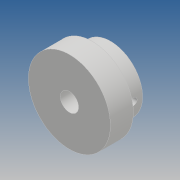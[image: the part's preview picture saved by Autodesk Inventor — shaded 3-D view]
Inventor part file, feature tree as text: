
AUTODESK INVENTOR PART (.ipt)
format: ipt  version: 2017 (Build 210142000, 142)  size: 162,816 bytes
history: native  units: mm
features: extrude x4, sketch x3, other x1, projected_geometry x1
ambient origin geometry x8: Origin, YZ Plane, XZ Plane, XY Plane, X Axis, Y Axis, Z Axis, Center Point
bodies: Body1 (feature_tree)
feature tree (9):
  other  "Sólido1"
  extrude  "Extrusión1"  Depth=10.0mm
  sketch  "Boceto2"  dims[d3=5.0mm d4=3.0mm]
  extrude  "Extrusión2"  Depth=3.0mm
  extrude  "Extrusión3"  Depth=10.0mm
  extrude  "Extrusión4"  TaperAngle=120.0deg  [1 undecoded]
  sketch  "Boceto1"  dims[d0=8.0mm d2=10.0mm]
  projected_geometry  "Contorno proyectado1"
  sketch  "Boceto3"  dims[d5=8.0mm d6=0.0mm d7=3.2mm d8=120.0deg d9=2.95mm d10=15.0mm d11=0.0mm d12=4.0mm d13=0.0mm d14=10.0mm d15=0.0mm]
note: 1 required parameter value undecoded (feature->parameter linkage not recoverable at this tier; creation-order binding heuristic only, values carry confidence <= 0.55)
